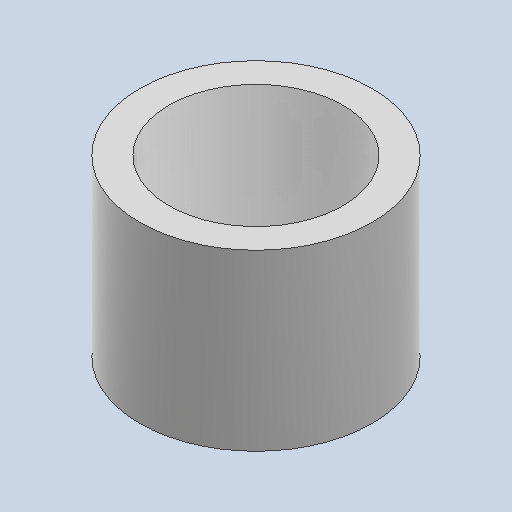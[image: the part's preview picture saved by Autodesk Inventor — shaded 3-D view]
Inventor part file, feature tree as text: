
AUTODESK INVENTOR PART (.ipt)
format: ipt  version: 2024.2 (Build 282272000, 272)  size: 207,360 bytes
history: native  units: mm
features: other x1, extrude x1, sketch x1
ambient origin geometry x8: Origin, YZ Plane, XZ Plane, XY Plane, X Axis, Y Axis, Z Axis, Center Point
bodies: Body1 (feature_tree)
feature tree (3):
  other  "Bryła1"
  extrude  "Wyciągnięcie proste1"  Depth=6.0mm
  sketch  "Szkic1"
